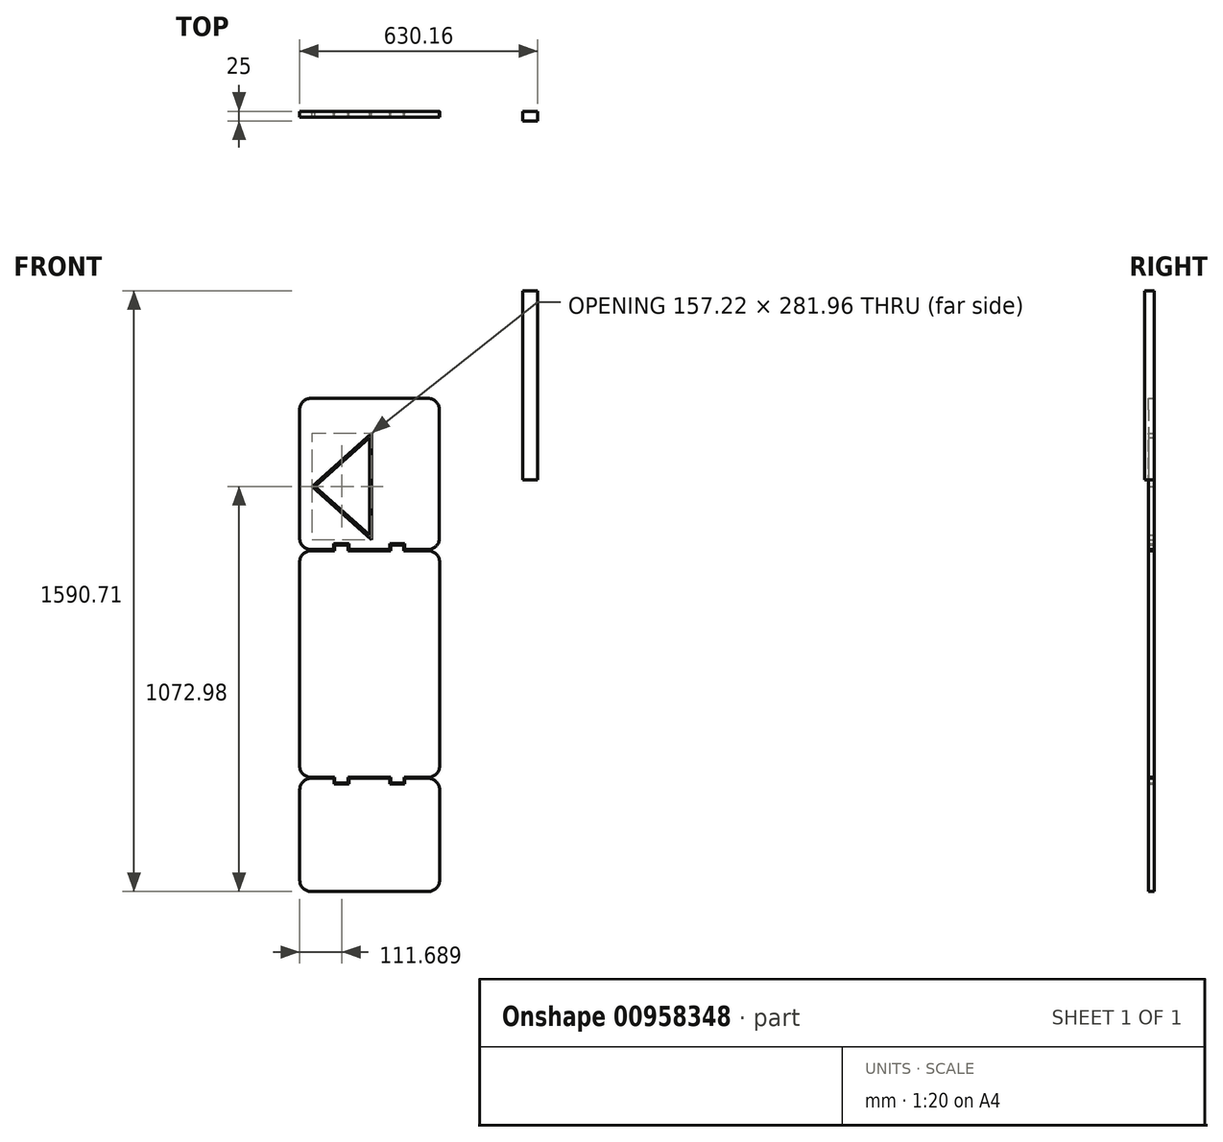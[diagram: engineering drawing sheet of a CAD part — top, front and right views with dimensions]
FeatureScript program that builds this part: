
annotation { "Feature Type Name" : "Feature", "Feature Type Description" : "" }
export const myFeature = defineFeature(function(context is Context, id is Id, definition is map)
    precondition{}
    {
        {
            var Q0;
            Q0=qCreatedBy(makeId("Front.planeOp"),FACE);
            var sketch = newSketch(context, id + "F0", { "sketchPlane" : qUnion([Q0])});
            skLineSegment(sketch, "E0.bottom", {"start": v(-152, 251.05) * mm, "end": v(158, 251.05) * mm});
            skLineSegment(sketch, "E0.top", {"start": v(-152, -148.95) * mm, "end": v(-91.48, -148.95) * mm});
            skLineSegment(sketch, "E0.left", {"start": v(-182, 221.05) * mm, "end": v(-182, -118.95) * mm});
            skLineSegment(sketch, "E0.right", {"start": v(188, 221.05) * mm, "end": v(188, -118.95) * mm});
            skPoint(sketch, "E1.visualSharp", {"position": v(-182, 251.05) * mm});
            skArc(sketch, "E1.filletArc", {"start": v(-152, 251.05) * mm, "mid": v(-173.22, 242.26) * mm, "end": v(-182, 221.05) * mm});
            skPoint(sketch, "E2.visualSharp", {"position": v(-182, -148.95) * mm});
            skArc(sketch, "E2.filletArc", {"start": v(-182, -118.95) * mm, "mid": v(-173.22, -140.16) * mm, "end": v(-152, -148.95) * mm});
            skPoint(sketch, "E3.visualSharp", {"position": v(188, -148.95) * mm});
            skArc(sketch, "E3.filletArc", {"start": v(158, -148.95) * mm, "mid": v(179.2, -140.16) * mm, "end": v(188, -118.95) * mm});
            skPoint(sketch, "E4.visualSharp", {"position": v(188, 251.05) * mm});
            skArc(sketch, "E4.filletArc", {"start": v(188, 221.05) * mm, "mid": v(179.2, 242.26) * mm, "end": v(158, 251.05) * mm});
            skPoint(sketch, "E5.orphan", {"position": v(3, 251.05) * mm});
            skPoint(sketch, "E6.orphan", {"position": v(3, -148.95) * mm});
            skLineSegment(sketch, "E7.bottom", {"start": v(-91.48, -133.95) * mm, "end": v(-51.48, -133.95) * mm});
            skLineSegment(sketch, "E7.left", {"start": v(-91.48, -133.95) * mm, "end": v(-91.48, -148.95) * mm});
            skLineSegment(sketch, "E7.right", {"start": v(-51.48, -133.95) * mm, "end": v(-51.48, -148.95) * mm});
            skLineSegment(sketch, "E8.bottom", {"start": v(56.42, -133.95) * mm, "end": v(96.42, -133.95) * mm});
            skLineSegment(sketch, "E8.left", {"start": v(56.42, -133.95) * mm, "end": v(56.42, -148.95) * mm});
            skLineSegment(sketch, "E8.right", {"start": v(96.42, -133.95) * mm, "end": v(96.42, -148.95) * mm});
            skLineSegment(sketch, "E9.bottom", {"start": v(408.15, 536) * mm, "end": v(448.15, 536) * mm});
            skLineSegment(sketch, "E9.top", {"start": v(408.15, 36) * mm, "end": v(448.15, 36) * mm});
            skLineSegment(sketch, "E9.left", {"start": v(408.15, 536) * mm, "end": v(408.15, 36) * mm});
            skLineSegment(sketch, "E9.right", {"start": v(448.15, 536) * mm, "end": v(448.15, 36) * mm});
            skLineSegment(sketch, "E10.trimOffspring", {"start": v(-51.48, -148.95) * mm, "end": v(56.42, -148.95) * mm});
            skLineSegment(sketch, "E11.trimOffspring", {"start": v(96.42, -148.95) * mm, "end": v(158, -148.95) * mm});
            skLineSegment(sketch, "E12.bottom", {"start": v(-151.65, -152.29) * mm, "end": v(-89.06, -152.29) * mm});
            skLineSegment(sketch, "E12.top", {"start": v(-151.65, -752.29) * mm, "end": v(-88.9, -752.29) * mm});
            skLineSegment(sketch, "E12.left", {"start": v(-181.65, -182.29) * mm, "end": v(-181.65, -722.29) * mm});
            skLineSegment(sketch, "E12.right", {"start": v(188.35, -182.29) * mm, "end": v(188.35, -722.29) * mm});
            skPoint(sketch, "E13.visualSharp", {"position": v(-181.65, -152.29) * mm});
            skArc(sketch, "E13.filletArc", {"start": v(-151.65, -152.29) * mm, "mid": v(-172.86, -161.07) * mm, "end": v(-181.65, -182.29) * mm});
            skPoint(sketch, "E14.visualSharp", {"position": v(-181.65, -752.29) * mm});
            skArc(sketch, "E14.filletArc", {"start": v(-181.65, -722.29) * mm, "mid": v(-172.86, -743.5) * mm, "end": v(-151.65, -752.29) * mm});
            skPoint(sketch, "E15.visualSharp", {"position": v(188.35, -752.29) * mm});
            skArc(sketch, "E15.filletArc", {"start": v(158.35, -752.29) * mm, "mid": v(179.56, -743.5) * mm, "end": v(188.35, -722.29) * mm});
            skPoint(sketch, "E16.visualSharp", {"position": v(188.35, -152.29) * mm});
            skArc(sketch, "E16.filletArc", {"start": v(188.35, -182.29) * mm, "mid": v(179.56, -161.07) * mm, "end": v(158.35, -152.29) * mm});
            skPoint(sketch, "E17.orphan", {"position": v(3.35, -152.29) * mm});
            skLineSegment(sketch, "E18.trimOffspring", {"start": v(-53.9, -752.29) * mm, "end": v(59.34, -752.29) * mm});
            skLineSegment(sketch, "E19.trimOffspring", {"start": v(94.34, -752.29) * mm, "end": v(158.35, -752.29) * mm});
            skLineSegment(sketch, "E20.bottom", {"start": v(355.64, -74.44) * mm, "end": v(390.64, -74.44) * mm});
            skLineSegment(sketch, "E20.top", {"start": v(355.64, -89.44) * mm, "end": v(390.64, -89.44) * mm});
            skLineSegment(sketch, "E20.left", {"start": v(355.64, -74.44) * mm, "end": v(355.64, -89.44) * mm});
            skLineSegment(sketch, "E20.right", {"start": v(390.64, -74.44) * mm, "end": v(390.64, -89.44) * mm});
            skLineSegment(sketch, "E21.bottom", {"start": v(-89.06, -137.29) * mm, "end": v(-54.06, -137.29) * mm});
            skLineSegment(sketch, "E21.left", {"start": v(-89.06, -137.29) * mm, "end": v(-89.06, -152.29) * mm});
            skLineSegment(sketch, "E21.right", {"start": v(-54.06, -137.29) * mm, "end": v(-54.06, -152.29) * mm});
            skLineSegment(sketch, "E22.bottom", {"start": v(59.11, -137.29) * mm, "end": v(94.11, -137.29) * mm});
            skLineSegment(sketch, "E22.left", {"start": v(59.11, -137.29) * mm, "end": v(59.11, -152.29) * mm});
            skLineSegment(sketch, "E22.right", {"start": v(94.11, -137.29) * mm, "end": v(94.11, -152.29) * mm});
            skLineSegment(sketch, "E23.trimOffspring", {"start": v(-54.06, -152.29) * mm, "end": v(59.11, -152.29) * mm});
            skLineSegment(sketch, "E24.trimOffspring", {"start": v(94.11, -152.29) * mm, "end": v(158.35, -152.29) * mm});
            skLineSegment(sketch, "E25.bottom", {"start": v(-151.6, -754.71) * mm, "end": v(-91.26, -754.71) * mm});
            skLineSegment(sketch, "E25.top", {"start": v(-151.6, -1054.71) * mm, "end": v(-91.38, -1054.71) * mm});
            skLineSegment(sketch, "E25.left", {"start": v(-181.6, -784.71) * mm, "end": v(-181.6, -1024.71) * mm});
            skLineSegment(sketch, "E25.right", {"start": v(188.4, -784.71) * mm, "end": v(188.4, -1024.71) * mm});
            skPoint(sketch, "E26.visualSharp", {"position": v(-181.6, -754.71) * mm});
            skArc(sketch, "E26.filletArc", {"start": v(-151.6, -754.71) * mm, "mid": v(-172.81, -763.5) * mm, "end": v(-181.6, -784.71) * mm});
            skPoint(sketch, "E27.visualSharp", {"position": v(-181.6, -1054.71) * mm});
            skArc(sketch, "E27.filletArc", {"start": v(-181.6, -1024.71) * mm, "mid": v(-172.81, -1045.93) * mm, "end": v(-151.6, -1054.71) * mm});
            skPoint(sketch, "E28.visualSharp", {"position": v(188.4, -1054.71) * mm});
            skArc(sketch, "E28.filletArc", {"start": v(158.4, -1054.71) * mm, "mid": v(179.61, -1045.93) * mm, "end": v(188.4, -1024.71) * mm});
            skPoint(sketch, "E29.visualSharp", {"position": v(188.4, -754.71) * mm});
            skArc(sketch, "E29.filletArc", {"start": v(188.4, -784.71) * mm, "mid": v(179.61, -763.5) * mm, "end": v(158.4, -754.71) * mm});
            skPoint(sketch, "E30.orphan", {"position": v(3.4, -754.71) * mm});
            skPoint(sketch, "E31.orphan", {"position": v(3.4, -1054.71) * mm});
            skLineSegment(sketch, "E32.trimOffspring", {"start": v(-91.38, -1054.71) * mm, "end": v(56.52, -1054.71) * mm});
            skLineSegment(sketch, "E33.trimOffspring", {"start": v(56.52, -1054.71) * mm, "end": v(158.4, -1054.71) * mm});
            skLineSegment(sketch, "E34.top", {"start": v(56.47, -769.71) * mm, "end": v(96.47, -769.71) * mm});
            skLineSegment(sketch, "E34.left", {"start": v(56.47, -754.71) * mm, "end": v(56.47, -769.71) * mm});
            skLineSegment(sketch, "E34.right", {"start": v(96.47, -754.71) * mm, "end": v(96.47, -769.71) * mm});
            skLineSegment(sketch, "E35.top", {"start": v(-88.9, -767.29) * mm, "end": v(-53.9, -767.29) * mm});
            skLineSegment(sketch, "E35.left", {"start": v(-88.9, -752.29) * mm, "end": v(-88.9, -767.29) * mm});
            skLineSegment(sketch, "E35.right", {"start": v(-53.9, -752.29) * mm, "end": v(-53.9, -767.29) * mm});
            skLineSegment(sketch, "E36.top", {"start": v(59.34, -767.29) * mm, "end": v(94.34, -767.29) * mm});
            skLineSegment(sketch, "E36.left", {"start": v(59.34, -752.29) * mm, "end": v(59.34, -767.29) * mm});
            skLineSegment(sketch, "E36.right", {"start": v(94.34, -752.29) * mm, "end": v(94.34, -767.29) * mm});
            skLineSegment(sketch, "E37.top", {"start": v(-91.26, -769.7) * mm, "end": v(-51.26, -769.7) * mm});
            skLineSegment(sketch, "E37.left", {"start": v(-91.26, -754.7) * mm, "end": v(-91.26, -769.7) * mm});
            skLineSegment(sketch, "E37.right", {"start": v(-51.26, -754.7) * mm, "end": v(-51.26, -769.7) * mm});
            skLineSegment(sketch, "E38.trimOffspring", {"start": v(-51.26, -754.71) * mm, "end": v(56.47, -754.71) * mm});
            skLineSegment(sketch, "E39.trimOffspring", {"start": v(96.47, -754.71) * mm, "end": v(158.4, -754.71) * mm});
            skLineSegment(sketch, "E40", {"start": v(3, 147.39) * mm, "end": v(3, -110.85) * mm});
            skLineSegment(sketch, "E41", {"start": v(3, -110.85) * mm, "end": v(-141, 18.27) * mm});
            skPoint(sketch, "E41.endSnap0", {"position": v(3, 18.27) * mm});
            skLineSegment(sketch, "E42", {"start": v(-141, 18.27) * mm, "end": v(3, 147.39) * mm});
            skLineSegment(sketch, "E43.0", {"start": v(8.29, -122.7) * mm, "end": v(-148.93, 18.27) * mm});
            skLineSegment(sketch, "E43.1", {"start": v(8.29, 159.25) * mm, "end": v(8.29, -122.7) * mm});
            skLineSegment(sketch, "E43.2", {"start": v(-148.93, 18.27) * mm, "end": v(8.29, 159.25) * mm});
            skSolve(sketch);
        }
        {
            var Q0;
            Q0=makeQuery(id+"F0.imprint","IMPRINT",FACE,{"disambiguationData":[TD([[makeQuery(id+"F0.imprint","IMPRINT",EDGE,{"derivedFrom":sQuery(id+"F0.wireOp",EDGE,"E0.bottom")}),-1.0]])]});
            var Q1;
            Q1=makeQuery(id+"F0.imprint","IMPRINT",FACE,{"disambiguationData":[TD([[makeQuery(id+"F0.imprint","IMPRINT",EDGE,{"derivedFrom":sQuery(id+"F0.wireOp",EDGE,"d466acea-3703-408c-b262-50067e0f1df2.0")}),1.0]])]});
            extrude(context, id + "F1", {"entities" : qUnion([Q0, Q1]), "depth" : 15 * mm, "offsetDistance" : 25 * mm});
        }
        {
            var Q0;
            Q0=makeQuery(id+"F0.imprint","IMPRINT",FACE,{"disambiguationData":[TD([[makeQuery(id+"F0.imprint","IMPRINT",EDGE,{"derivedFrom":sQuery(id+"F0.wireOp",EDGE,"E12.bottom")}),-1.0]])]});
            var Q1;
            Q1=makeQuery(id+"F0.imprint","IMPRINT",FACE,{"disambiguationData":[TD([[makeQuery(id+"F0.imprint","IMPRINT",EDGE,{"derivedFrom":sQuery(id+"F0.wireOp",EDGE,"E25.bottom")}),-1.0]])]});
            var Q2;
            Q2=makeQuery(id+"F0.imprint","IMPRINT",FACE,{"disambiguationData":[TD([[makeQuery(id+"F0.imprint","IMPRINT",EDGE,{"derivedFrom":sQuery(id+"F0.wireOp",EDGE,"E40")}),-1.0]])]});
            extrude(context, id + "F2", {"entities" : qUnion([Q0, Q1, Q2]), "depth" : 15 * mm, "offsetDistance" : 25 * mm});
        }
        {
            var Q0;
            Q0=makeQuery(id+"F0.imprint","IMPRINT",FACE,{"disambiguationData":[TD([[makeQuery(id+"F0.imprint","IMPRINT",EDGE,{"derivedFrom":sQuery(id+"F0.wireOp",EDGE,"E9.bottom")}),-1.0]])]});
            extrude(context, id + "F3", {"entities" : qUnion([Q0]), "depth" : 25 * mm, "offsetDistance" : 25 * mm});
        }
    });
